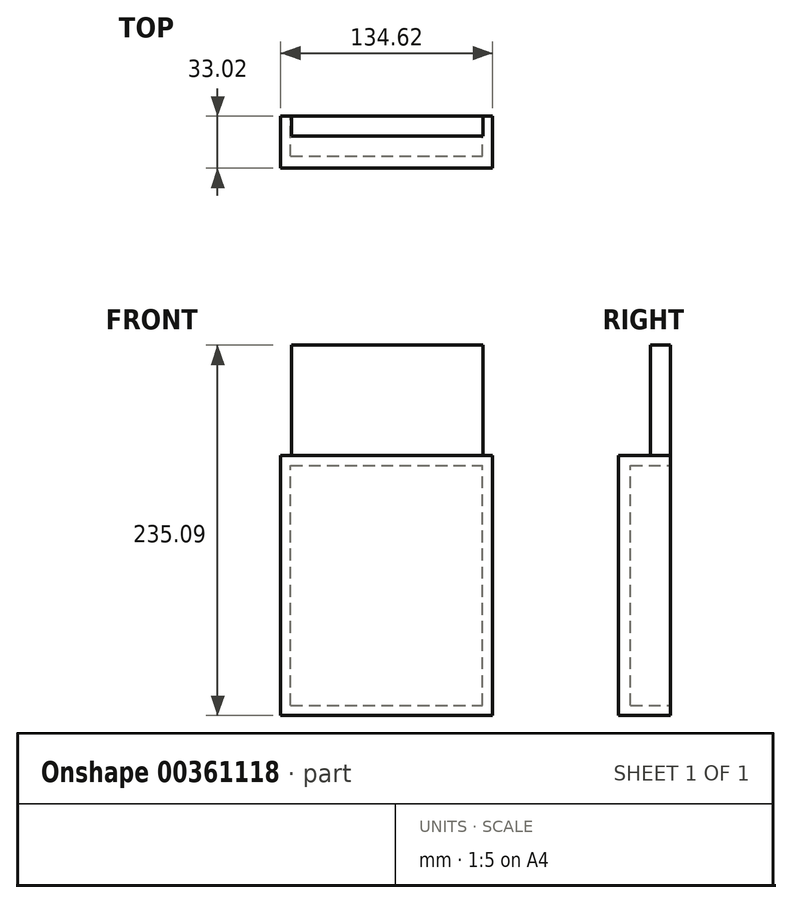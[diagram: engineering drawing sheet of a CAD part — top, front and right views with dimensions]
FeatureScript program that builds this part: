
annotation { "Feature Type Name" : "Feature", "Feature Type Description" : "" }
export const myFeature = defineFeature(function(context is Context, id is Id, definition is map)
    precondition{}
    {
        {
            var Q0;
            Q0=qCreatedBy(makeId("Front.planeOp"),FACE);
            var sketch = newSketch(context, id + "F0", { "sketchPlane" : qUnion([Q0])});
            skLineSegment(sketch, "E0.bottom", {"start": v(0, 0) * mm, "end": v(134.62, 0) * mm});
            skLineSegment(sketch, "E0.top", {"start": v(0, 165.1) * mm, "end": v(134.62, 165.1) * mm});
            skLineSegment(sketch, "E0.left", {"start": v(0, 0) * mm, "end": v(0, 165.1) * mm});
            skLineSegment(sketch, "E0.right", {"start": v(134.62, 0) * mm, "end": v(134.62, 165.1) * mm});
            skLineSegment(sketch, "E1.0", {"start": v(6.35, 158.75) * mm, "end": v(128.27, 158.75) * mm});
            skLineSegment(sketch, "E1.1", {"start": v(6.35, 6.35) * mm, "end": v(6.35, 158.75) * mm});
            skLineSegment(sketch, "E1.2", {"start": v(6.35, 6.35) * mm, "end": v(128.27, 6.35) * mm});
            skLineSegment(sketch, "E1.3", {"start": v(128.27, 6.35) * mm, "end": v(128.27, 158.75) * mm});
            skSolve(sketch);
        }
        {
            var Q0;
            Q0=makeQuery(id+"F0.imprint","IMPRINT",FACE,{"disambiguationData":[TD([[makeQuery(id+"F0.imprint","IMPRINT",EDGE,{"derivedFrom":sQuery(id+"F0.wireOp",EDGE,"E0.bottom")}),1.0]])]});
            extrude(context, id + "F1", {"entities" : qUnion([Q0]), "depth" : 33.02 * mm});
        }
        {
            var Q0;
            Q0=makeQuery(id+"F1.opExtrude","CAP_FACE",FACE,{"disambiguationData":[OSD([sQuery(id+"F0.wireOp",EDGE,"E0.bottom"),sQuery(id+"F0.wireOp",EDGE,"E0.top"),sQuery(id+"F0.wireOp",EDGE,"E0.left"),sQuery(id+"F0.wireOp",EDGE,"E0.right"),sQuery(id+"F0.wireOp",EDGE,"E1.0"),sQuery(id+"F0.wireOp",EDGE,"E1.1"),sQuery(id+"F0.wireOp",EDGE,"E1.2"),sQuery(id+"F0.wireOp",EDGE,"E1.3")])],"isStart":false});
            var sketch = newSketch(context, id + "F2", { "sketchPlane" : qUnion([Q0])});
            skLineSegment(sketch, "E2.bottom", {"start": v(6.35, 158.75) * mm, "end": v(128.27, 158.75) * mm});
            skLineSegment(sketch, "E2.top", {"start": v(6.35, 6.35) * mm, "end": v(128.27, 6.35) * mm});
            skLineSegment(sketch, "E2.left", {"start": v(6.35, 158.75) * mm, "end": v(6.35, 6.35) * mm});
            skLineSegment(sketch, "E2.right", {"start": v(128.27, 158.75) * mm, "end": v(128.27, 6.35) * mm});
            skSolve(sketch);
        }
        {
            var Q0;
            Q0=makeQuery(id+"F1.opExtrude","CAP_FACE",FACE,{"disambiguationData":[OSD([sQuery(id+"F0.wireOp",EDGE,"E0.bottom"),sQuery(id+"F0.wireOp",EDGE,"E0.top"),sQuery(id+"F0.wireOp",EDGE,"E0.left"),sQuery(id+"F0.wireOp",EDGE,"E0.right"),sQuery(id+"F0.wireOp",EDGE,"E1.0"),sQuery(id+"F0.wireOp",EDGE,"E1.1"),sQuery(id+"F0.wireOp",EDGE,"E1.2"),sQuery(id+"F0.wireOp",EDGE,"E1.3")])],"isStart":true});
            var sketch = newSketch(context, id + "F3", { "sketchPlane" : qUnion([Q0])});
            skLineSegment(sketch, "E3.bottom", {"start": v(-128.27, 158.75) * mm, "end": v(-6.35, 158.75) * mm});
            skLineSegment(sketch, "E3.top", {"start": v(-128.27, 6.35) * mm, "end": v(-6.35, 6.35) * mm});
            skLineSegment(sketch, "E3.left", {"start": v(-128.27, 158.75) * mm, "end": v(-128.27, 6.35) * mm});
            skLineSegment(sketch, "E3.right", {"start": v(-6.35, 158.75) * mm, "end": v(-6.35, 6.35) * mm});
            skSolve(sketch);
        }
        {
            var Q0;
            Q0=makeQuery(id+"F2.imprint","IMPRINT",FACE,{"disambiguationData":[TD([[makeQuery(id+"F2.imprint","IMPRINT",EDGE,{"derivedFrom":sQuery(id+"F2.wireOp",EDGE,"E2.bottom")}),-1.0]])]});
            extrude(context, id + "F4", {"entities" : qUnion([Q0]), "operationType" : NewBodyOperationType.ADD, "oppositeDirection" : true, "depth" : 7.62 * mm});
        }
        {
            var Q0;
            Q0=makeQuery(id+"F3.imprint","IMPRINT",FACE,{"disambiguationData":[TD([[makeQuery(id+"F3.imprint","IMPRINT",EDGE,{"derivedFrom":sQuery(id+"F3.wireOp",EDGE,"E3.bottom")}),-1.0]])]});
            var sketch = newSketch(context, id + "F5", { "sketchPlane" : qUnion([Q0])});
            skLineSegment(sketch, "E4.bottom", {"start": v(-128.41, 158.89) * mm, "end": v(-6.74, 158.89) * mm});
            skLineSegment(sketch, "E4.top", {"start": v(-128.41, 235.09) * mm, "end": v(-6.74, 235.09) * mm});
            skLineSegment(sketch, "E4.left", {"start": v(-128.41, 158.89) * mm, "end": v(-128.41, 235.09) * mm});
            skLineSegment(sketch, "E4.right", {"start": v(-6.74, 158.89) * mm, "end": v(-6.74, 235.09) * mm});
            skSolve(sketch);
        }
        {
            var Q0;
            {var subQ0=sQuery(id+"F5.wireOp",EDGE,"E4.top");Q0=makeQuery(id+"F5.imprint","IMPRINT",FACE,{"disambiguationData":[TD([[makeQuery(id+"F5.imprint","IMPRINT",EDGE,{"derivedFrom":subQ0}),-1.0]])]});}
            extrude(context, id + "F6", {"entities" : qUnion([Q0]), "operationType" : NewBodyOperationType.ADD, "oppositeDirection" : true, "depth" : 12.7 * mm});
        }
        {
            var Q0;
            Q0=makeQuery(id+"F1.opExtrude","SWEPT_FACE",FACE,{"disambiguationData":[OSD([sQuery(id+"F0.wireOp",EDGE,"E0.bottom")])]});
            extrude(context, id + "F7", {"entities" : qUnion([Q0]), "operationType" : NewBodyOperationType.ADD, "oppositeDirection" : true, "depth" : 5.08 * mm});
        }
        {
            var Q0;
            Q0=makeQuery(id+"F1.opExtrude","SWEPT_FACE",FACE,{"disambiguationData":[OSD([sQuery(id+"F0.wireOp",EDGE,"E0.bottom")])]});
            extrude(context, id + "F8", {"entities" : qUnion([Q0]), "operationType" : NewBodyOperationType.ADD, "oppositeDirection" : true, "depth" : 3.8 * mm});
        }
    });
